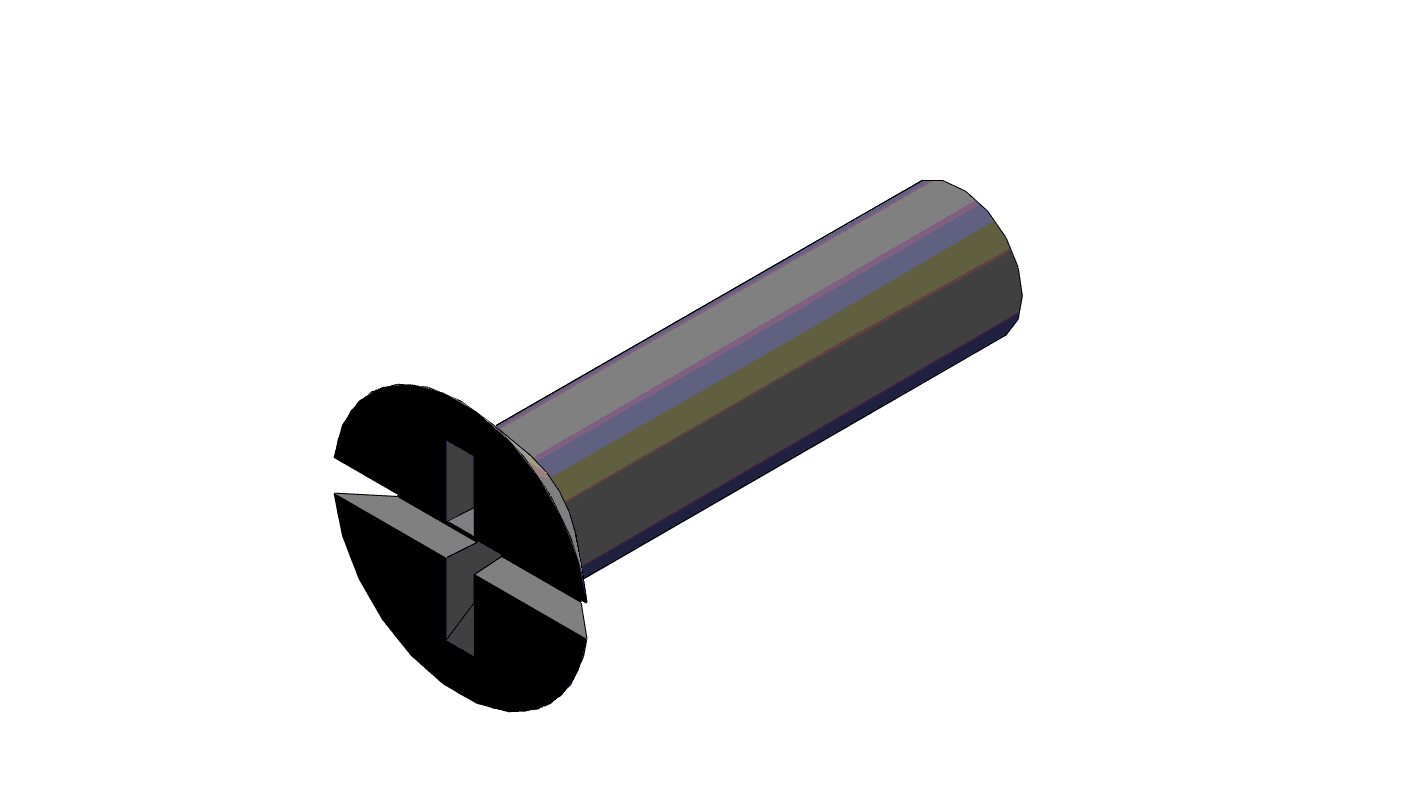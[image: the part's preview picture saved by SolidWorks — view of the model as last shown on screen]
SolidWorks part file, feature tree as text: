
SOLIDWORKS PART (.sldprt)
format: sldprt  version: not decoded by parser v0  size: 776,192 bytes
history: native  units: mm
features: sketch x5, plane x4, material x1, revolve x1, thread x1, cut_extrude x1, pattern_circular x1, cut_revolve x1, pattern_linear x1 (+8 scaffold rows collapsed)
feature tree (24):
  scaffold x8  (default folders/planes/origin — collapsed)
  material  "Material <not specified>"
  plane  "Plane1"
  plane  "Plane2"
  plane  "Plane3"
  sketch  "BodySke"  dims[c1.Diameter=9.525mm c1.D2=76.2mm c1.D3=5.842mm c1.D4=~18.513272mm c2.D4=82.0deg c2.D5=~19.681746mm c3.D4=19.3548mm c3.D5=~7.740726mm c4.D5=~80.148096deg c4.Length=38.1mm c4.Head_ht=4.191mm c4.Head_dia=19.3548mm c5.D5=~8.373577mm c5.Head_ang=100.0deg c5.D6=~0.066909mm c5.D7=88.9mm c5.Advance=1.5875mm c5.Thread_nom=31.75mm c5.Thread_lim=30.6705mm]
  revolve  "Base-Revolve"  [1 undecoded]
  thread  "ThreadCosmetic"  Diameter=31.75mm Thread_length=31.75mm Thread_minor=7.9248mm  [1 undecoded]
  sketch  "Sketch2"  dims[Slot_width=2.3876mm D1=1.1938mm D2=19.3548mm D3=9.6774mm]
  cut_extrude  "Slot"  Depth=2.2352mm Slot_depth=2.2352mm
  sketch  "Sketch3"  dims[c1.Cross_dia=12.9286mm c1.Cross_width=2.1844mm c1.D3=3.175mm c1.D4=6.4643mm c1.D5=3.175mm c1.D6=6.35mm c2.D6=90.0deg c3.D6=12.9286mm c3.D7=2.1844mm c3.D8=6.4643mm c3.Cross_dia=19.05mm c3.D1=19.05mm c3.Cross_width=6.35mm c3.D2=6.35mm c3.D3=9.525mm c3.D4=9.525mm c3.D5=3.175mm c4.D6=3.175mm c4.D7=6.35mm c4.D8=6.35mm c4.Cross_dia=13.2842mm c4.Cross_width=2.1844mm c4.D1=6.6421mm c4.D2=1.0922mm]
  plane  "Plane4"  Offset=7.9756mm Cross_depth=7.9756mm
  sketch  "Sketch4"  dims[c1.D1=~2.615571mm c1.D2=2.1844mm c2.D1=1.0922mm c2.D2=1.0922mm c2.D3=0.5461mm c2.D4=0.5461mm]
  pattern_circular  "CirPattern1"  Count=2 Angle=90deg
  sketch  "ThdSchSke"  dims[c1.Thread_minor=~1.03886mm c1.Diameter=~1.413535mm c1.Start=~0.988134mm c1.D4=~4.446753mm c1.Vee=60.0deg c2.Thread_minor=~1.03886mm c2.Start=~2.540025mm c2.D1=~0.108159mm c2.D2=~0.108159mm c3.D1=~0.216319mm c3.SideAngle=55.0deg c3.D2=~0.216319mm c3.VeeAngle=70.0deg c3.Thread_minor=7.9248mm c3.Overcut=~11.90625mm c3.Diameter=9.525mm c3.D6=~8.326268mm c4.D1=~8.326268mm c5.D1=90.0deg c5.Start=11.1125mm c6.Start=~44.450025mm c7.Start=~6.350025mm]
  cut_revolve  "ThreadSchematic"  Angle=360deg
  pattern_linear  "ThdSchPat"  Count1=21 Count2=1 Spacing1=1.5875mm Spacing2=50mm Num_threads=21 Advance=1.5875mm
decode coverage: 10 of 11 modeling features carry decoded parameters
note: ~ marks probable driven/reference dimensions
note: 2 parameter values undecoded
note: suppression state not decoded; provenance and decode notes live in map.json
